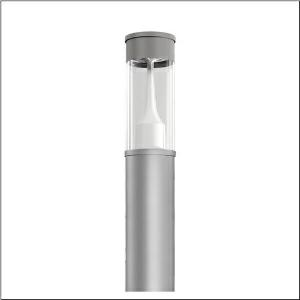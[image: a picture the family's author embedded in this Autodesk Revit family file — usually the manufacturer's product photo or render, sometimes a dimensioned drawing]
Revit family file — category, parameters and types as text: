
# Revit family: city-light_400_iq___p1_0a_5xa5305ff14hp_6c14
name_source: partatom
category: Lighting Fixtures
units: mm (PartAtom-declared; Revit-internal decimal feet)

## family parameters
Cut with Voids When Loaded = No
Host = Face
Light Source = No
Part Type = Normal
Room Calculation Point = No
Round Connector Dimension = Use Diameter
Shared = No

## types (1)
- --- (1 x LED, 4700 lm, 33.6 W, 3000K)
    Apparent Load = 34 VA
    CIE Flux Codes = 31 62 91 95 100
    Color Rendering = 70
    Color Temperature = 3000K
    Default Elevation = 1800 mm
    Description = City-Light 400 iQ, light pillar, Module 540 iQ-SR, primary light control with 3 zone facetted reflector, of plastic, silver coated, highly specular, structured, primary optical cover: cover, of PMMA, transparent, partly coated, light distribution: P1.0a, primary light characteristic: strongly asymmetric, LED, High Power LED, rated luminous flux: 4.700lm, luminous efficacy: 140lm/W, light colour: 730, colour temperature: 3000K, control gear: ECG iQ, control: presetting dimming logarithmic, Street-Remote, Auto-Match, Temp-Guard, Lumen-Switch, Night-Set, Smart-Wire, Light-Fading, Desk-Remote (wireless, voltage-free reading and setting of iQ features in the workshop via application-optimized NFC function/RFID function), optimised constant luminous flux control (CLO 2.0), with terminal, 6-pole, max. 2.5mm², mains connection: 230..240V, AC, 50/60Hz, start of lifetime: 34W, end of service life: 36W, reduction: 15W, luminaire housing, cylindrical, of extruded aluminium section, coated, Siteco® metallic grey (DB 702S), length: 4.694mm, diameter: 200mm, Module 540 iQ-SR, traffic white (RAL 9016), equipment: Power, protection rating (complete): IP65, insulation class (complete): insulation class II (safety insulation), certification: CE, ENEC, VDE, packaging unit: 1 piece

Light Distribution: P1.0a
    Height = 500 mm
    Lamp = 1 x LED
    Lamp Light Flux = 4700 lm
    Lamp Power = 33.6 W
    Lamp count = 1
    Length = 200 mm  [stored 0.656168 ft]
    Luminous efficacy = 140 lm/W
    Manufacturer = Siteco
    ModVariant = No
    Model = 5XA5305FF14HP
    Mounting Place = Floor
    Mounting Type = Freestanding
    Number of Poles = 1
    OnlyDefault = Yes
    Power Factor = 1
    Product Name = City-Light 400 iQ | P1.0a
    Product group = light pillar
    ProductGroupID = 1303
    Protection Class = Protection class II
    Protection Degree = IP 65
    RLX_Detail_Level = 1
    RLX_Emergency_Light_Flux = 0 lm
    RLX_Emergency_Type = 0
    RLX_Emergency_Type_DB = No
    RlxData = <blob elided: 53177 chars, md5=ab63491b>
    Socket = socket
    Standby Power = 0 W
    System Light Flux = 4700 lm
    System Power = 34 W
    Type Comments = factory setting: luminous flux: 100 % | dim-lin: 254 | 695 mA
    Type Image = l_1006916.jpg
    URL = http://relux.com
    VarID = @adj_127183
    Voltage = 0 V
    Weight = 0.00 kg
    Width = 0 mm  [stored 0 ft]

note: [stored X ft] marks values corroborated as IEEE doubles in the binary element streams (Revit-internal decimal feet)

## geometry (parser evidence)
native form markers: Blend x4, Sweep x11
no freeform markers — native parametric forms only
